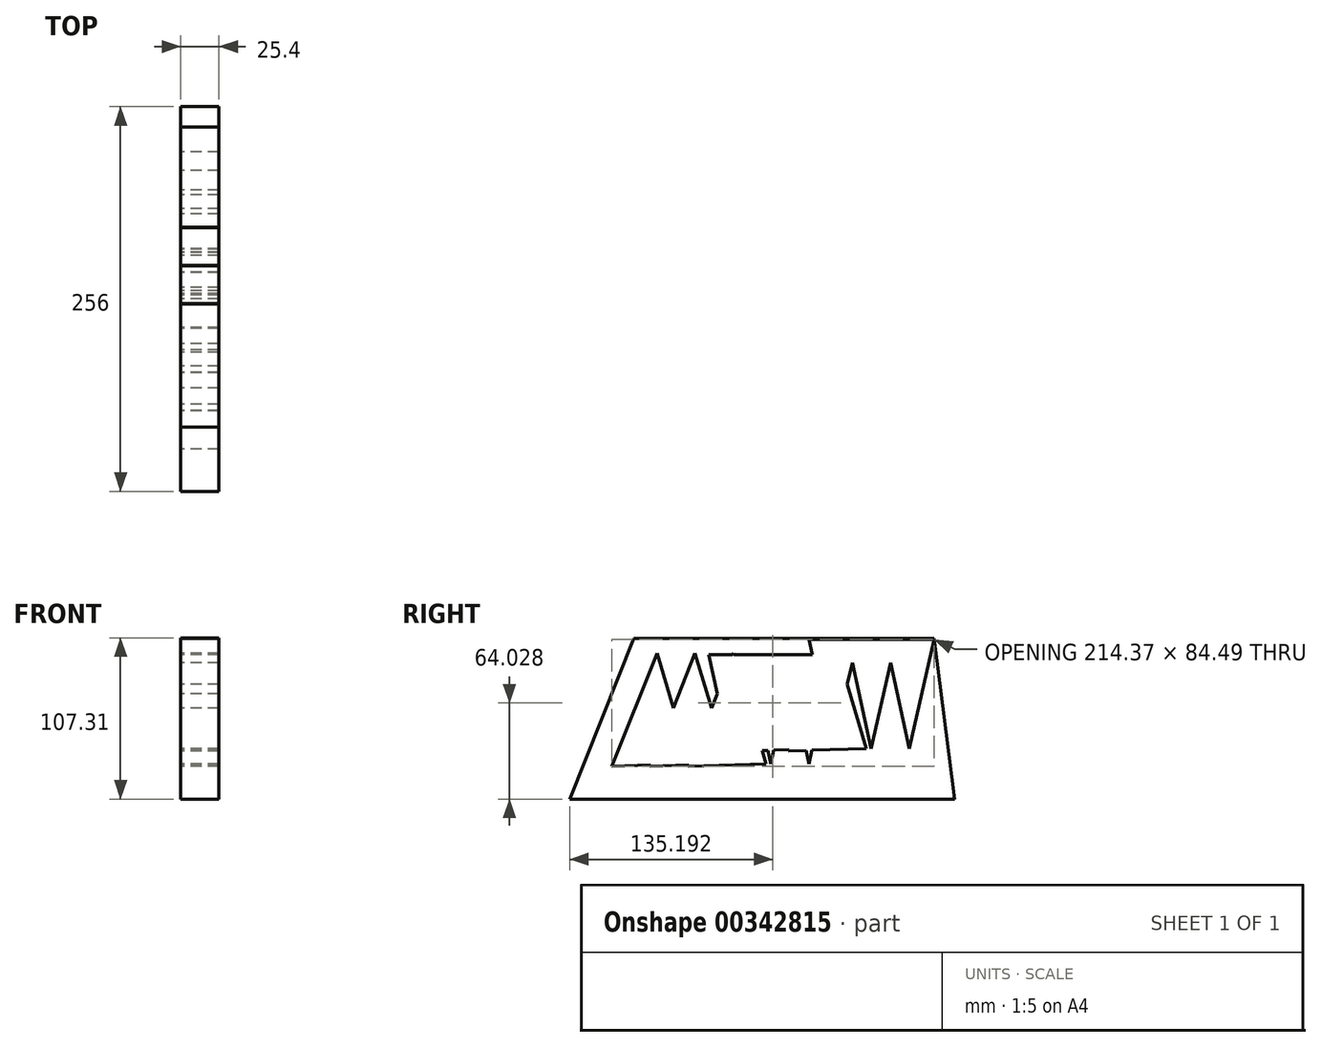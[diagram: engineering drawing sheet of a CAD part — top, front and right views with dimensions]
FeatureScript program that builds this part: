
annotation { "Feature Type Name" : "Feature", "Feature Type Description" : "" }
export const myFeature = defineFeature(function(context is Context, id is Id, definition is map)
    precondition{}
    {
        {
            var Q0;
            Q0=qCreatedBy(makeId("Right.planeOp"),FACE);
            var sketch = newSketch(context, id + "F0", { "sketchPlane" : qUnion([Q0])});
            skLineSegment(sketch, "E0", {"start": v(131.11, 0) * mm, "end": v(-124.89, 0) * mm});
            skLineSegment(sketch, "E1", {"start": v(-124.89, 0) * mm, "end": v(-82.17, 106.94) * mm});
            skLineSegment(sketch, "E2", {"start": v(-82.17, 106.94) * mm, "end": v(117.4, 106.94) * mm});
            skLineSegment(sketch, "E3", {"start": v(117.4, 106.94) * mm, "end": v(131.11, 0) * mm});
            skLineSegment(sketch, "E4", {"start": v(-96.88, 21.78) * mm, "end": v(-66.8, 97.09) * mm});
            skLineSegment(sketch, "E5", {"start": v(-66.8, 97.09) * mm, "end": v(-45.02, 23.44) * mm});
            skLineSegment(sketch, "E6", {"start": v(-45.02, 23.44) * mm, "end": v(-96.88, 21.78) * mm});
            skLineSegment(sketch, "E7", {"start": v(-32.36, 96.05) * mm, "end": v(0, 96.05) * mm});
            skLineSegment(sketch, "E8", {"start": v(0, 96.05) * mm, "end": v(-16.6, 23.44) * mm});
            skLineSegment(sketch, "E9", {"start": v(-16.6, 23.44) * mm, "end": v(-32.36, 96.05) * mm});
            skLineSegment(sketch, "E10.0.1.0", {"start": v(66.69, 106.27) * mm, "end": v(50.09, 33.66) * mm});
            skLineSegment(sketch, "E10.0.1.1", {"start": v(50.09, 33.66) * mm, "end": v(34.32, 106.27) * mm});
            skLineSegment(sketch, "E10.0.1.2", {"start": v(-30.2, 32) * mm, "end": v(-0.12, 107.3) * mm});
            skLineSegment(sketch, "E10.0.1.3", {"start": v(21.67, 33.66) * mm, "end": v(-30.2, 32) * mm});
            skLineSegment(sketch, "E10.0.1.4", {"start": v(34.32, 106.27) * mm, "end": v(66.69, 106.27) * mm});
            skLineSegment(sketch, "E10.0.1.5", {"start": v(-0.12, 107.3) * mm, "end": v(21.67, 33.66) * mm});
            skLineSegment(sketch, "E10.1.0.0", {"start": v(25.4, 96.05) * mm, "end": v(8.8, 23.44) * mm});
            skLineSegment(sketch, "E10.1.0.1", {"start": v(8.8, 23.44) * mm, "end": v(-6.96, 96.05) * mm});
            skLineSegment(sketch, "E10.1.0.2", {"start": v(-71.48, 21.78) * mm, "end": v(-41.4, 97.09) * mm});
            skLineSegment(sketch, "E10.1.0.3", {"start": v(-19.62, 23.44) * mm, "end": v(-71.48, 21.78) * mm});
            skLineSegment(sketch, "E10.1.0.4", {"start": v(-6.96, 96.05) * mm, "end": v(25.4, 96.05) * mm});
            skLineSegment(sketch, "E10.1.0.5", {"start": v(-41.4, 97.09) * mm, "end": v(-19.62, 23.44) * mm});
            skLineSegment(sketch, "E10.1.1.0", {"start": v(92.09, 106.27) * mm, "end": v(75.49, 33.66) * mm});
            skLineSegment(sketch, "E10.1.1.1", {"start": v(75.49, 33.66) * mm, "end": v(59.72, 106.27) * mm});
            skLineSegment(sketch, "E10.1.1.2", {"start": v(-4.8, 32) * mm, "end": v(25.28, 107.3) * mm});
            skLineSegment(sketch, "E10.1.1.3", {"start": v(47.07, 33.66) * mm, "end": v(-4.8, 32) * mm});
            skLineSegment(sketch, "E10.1.1.4", {"start": v(59.72, 106.27) * mm, "end": v(92.09, 106.27) * mm});
            skLineSegment(sketch, "E10.1.1.5", {"start": v(25.28, 107.3) * mm, "end": v(47.07, 33.66) * mm});
            skLineSegment(sketch, "E10.2.0.0", {"start": v(50.8, 96.05) * mm, "end": v(34.2, 23.44) * mm});
            skLineSegment(sketch, "E10.2.0.1", {"start": v(34.2, 23.44) * mm, "end": v(18.44, 96.05) * mm});
            skLineSegment(sketch, "E10.2.0.2", {"start": v(-46.08, 21.78) * mm, "end": v(-16, 97.09) * mm});
            skLineSegment(sketch, "E10.2.0.3", {"start": v(5.78, 23.44) * mm, "end": v(-46.08, 21.78) * mm});
            skLineSegment(sketch, "E10.2.0.4", {"start": v(18.44, 96.05) * mm, "end": v(50.8, 96.05) * mm});
            skLineSegment(sketch, "E10.2.0.5", {"start": v(-16, 97.09) * mm, "end": v(5.78, 23.44) * mm});
            skLineSegment(sketch, "E10.2.1.0", {"start": v(117.49, 106.27) * mm, "end": v(100.89, 33.66) * mm});
            skLineSegment(sketch, "E10.2.1.1", {"start": v(100.89, 33.66) * mm, "end": v(85.12, 106.27) * mm});
            skLineSegment(sketch, "E10.2.1.2", {"start": v(20.6, 32) * mm, "end": v(50.68, 107.3) * mm});
            skLineSegment(sketch, "E10.2.1.3", {"start": v(72.47, 33.66) * mm, "end": v(20.6, 32) * mm});
            skLineSegment(sketch, "E10.2.1.4", {"start": v(85.12, 106.27) * mm, "end": v(117.49, 106.27) * mm});
            skLineSegment(sketch, "E10.2.1.5", {"start": v(50.68, 107.3) * mm, "end": v(72.47, 33.66) * mm});
            skLineSegment(sketch, "E10.direction1", {"start": v(-96.88, 21.78) * mm, "end": v(-71.48, 21.78) * mm, "construction": true});
            skLineSegment(sketch, "E10.direction2", {"start": v(-96.88, 21.78) * mm, "end": v(-30.2, 32) * mm, "construction": true});
            skSolve(sketch);
        }
        {
            var Q0;
            Q0 = qSketchRegion(id + "F0", true);
            extrude(context, id + "F1", {"entities" : qUnion([Q0]), "depth" : 25.4 * mm});
        }
    });
